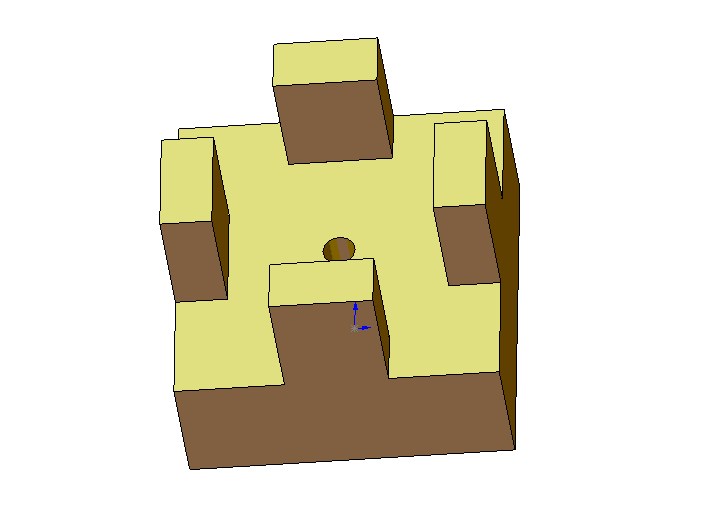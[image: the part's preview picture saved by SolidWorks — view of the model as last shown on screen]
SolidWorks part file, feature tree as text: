
SOLIDWORKS PART (.sldprt)
format: sldprt  version: not decoded by parser v0  size: 203,264 bytes
history: native  units: mm
features: sketch x3, extrude x2, cut_extrude x1 (+10 scaffold rows collapsed)
feature tree (16):
  scaffold x10  (default folders/planes/origin — collapsed)
  sketch  "Sketch1"  dims[D1=31.75mm D2=31.75mm]
  extrude  "Extrude1"  Depth=12.7mm
  sketch  "Sketch2"  dims[D1=10.16mm D2=5.08mm]
  extrude  "Extrude2"  Depth=12.7mm
  sketch  "Sketch3"  dims[D1=3.175mm]
  cut_extrude  "Cut-Extrude1"  [1 undecoded]
decode coverage: 5 of 6 modeling features carry decoded parameters
note: 1 parameter value undecoded
note: suppression state not decoded; provenance and decode notes live in map.json
